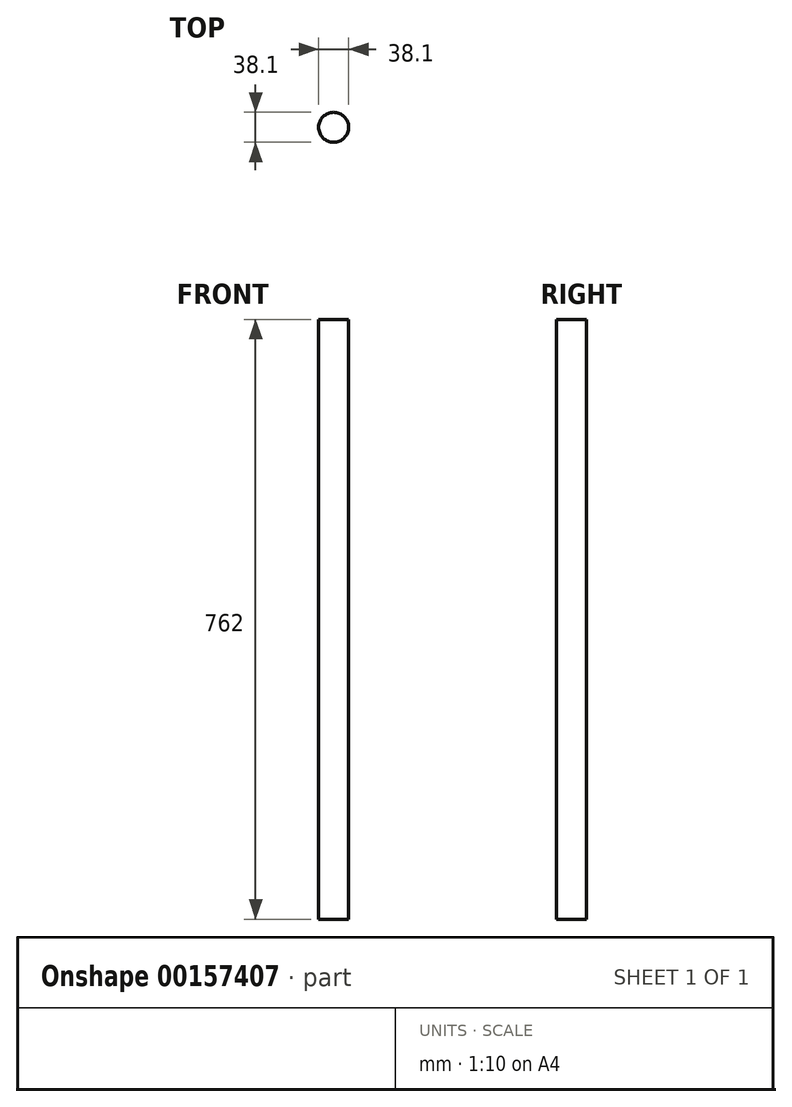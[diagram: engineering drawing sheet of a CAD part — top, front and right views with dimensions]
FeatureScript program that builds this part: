
annotation { "Feature Type Name" : "Feature", "Feature Type Description" : "" }
export const myFeature = defineFeature(function(context is Context, id is Id, definition is map)
    precondition{}
    {
        {
            var Q0;
            Q0=qCreatedBy(makeId("Top.planeOp"),FACE);
            var sketch = newSketch(context, id + "F0", { "sketchPlane" : qUnion([Q0])});
            skCircle(sketch, "E0", {"center": v(0, 0) * mm, "radius": 19.05 * mm});
            skSolve(sketch);
        }
        {
            var Q0;
            Q0 = qSketchRegion(id + "F0", true);
            extrude(context, id + "F1", {"entities" : qUnion([Q0]), "depth" : 762 * mm});
        }
    });
